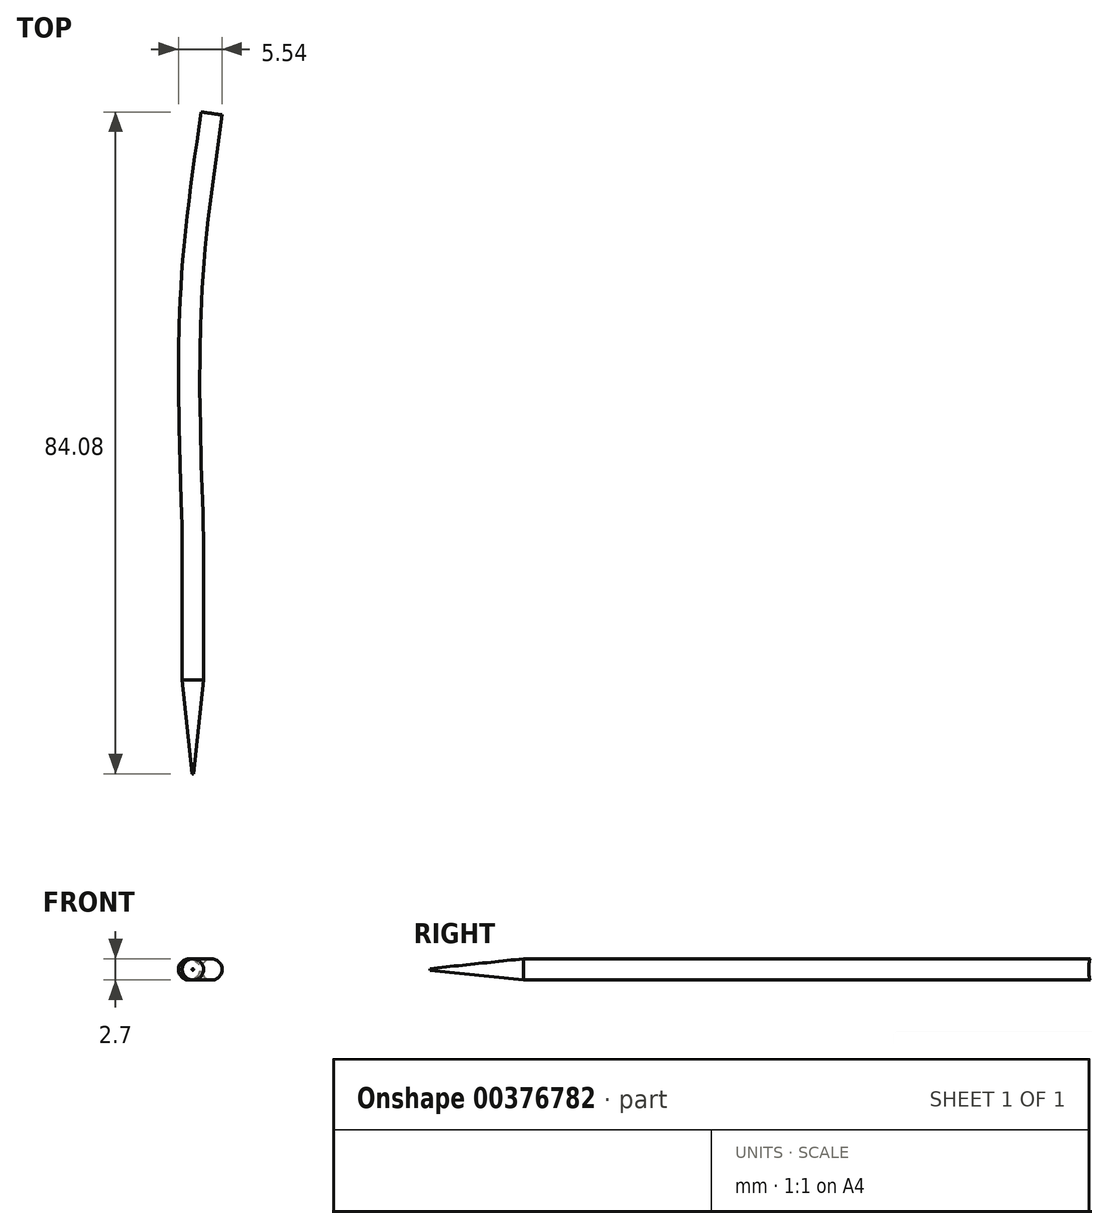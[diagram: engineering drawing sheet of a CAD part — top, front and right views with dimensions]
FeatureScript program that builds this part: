
annotation { "Feature Type Name" : "Feature", "Feature Type Description" : "" }
export const myFeature = defineFeature(function(context is Context, id is Id, definition is map)
    precondition{}
    {
        {
            var Q0;
            Q0=qCreatedBy(makeId("Front.planeOp"),FACE);
            var sketch = newSketch(context, id + "F0", { "sketchPlane" : qUnion([Q0])});
            skCircle(sketch, "E0", {"center": v(0, 0) * mm, "radius": 1.35 * mm});
            skCircle(sketch, "E1.0", {"center": v(0, 0) * mm, "radius": 0.1 * mm});
            skCircle(sketch, "E2.0", {"center": v(0, 0) * mm, "radius": 2.65 * mm});
            skSolve(sketch);
        }
        {
            var Q0;
            Q0=qCreatedBy(makeId("Top.planeOp"),FACE);
            var sketch = newSketch(context, id + "F1", { "sketchPlane" : qUnion([Q0])});
            skLineSegment(sketch, "E3", {"start": v(0, 0) * mm, "end": v(0, 30) * mm});
            skFitSpline(sketch, "E4", {"points": [v(0, 30) * mm, v(-0.41, 56.26) * mm, v(2.37, 83.9) * mm], "startDerivative": vector(0, 15.42) * mm, "endDerivative": vector(7.15, 51.63) * mm});
            skSolve(sketch);
        }
        {
            var Q0;
            Q0=makeQuery(id+"F0.imprint","IMPRINT",FACE,{"disambiguationData":[TD([[makeQuery(id+"F0.imprint","IMPRINT",EDGE,{"derivedFrom":sQuery(id+"F0.wireOp",EDGE,"E0")}),1.0]])]});
            var Q1;
            Q1=makeQuery(id+"F0.imprint","IMPRINT",FACE,{"disambiguationData":[TD([[makeQuery(id+"F0.imprint","IMPRINT",EDGE,{"derivedFrom":sQuery(id+"F0.wireOp",EDGE,"E1.0")}),1.0]])]});
            var Q2;
            Q2=sQuery(id+"F1.wireOp",EDGE,"E3");
            var Q3;
            Q3=sQuery(id+"F1.wireOp",EDGE,"E4");
            sweep(context, id + "F2", {"profiles" : qUnion([Q0, Q1]), "path" : qUnion([Q2, Q3])});
        }
        {
            var Q0;
            Q0=makeQuery(id+"F0.imprint","IMPRINT",FACE,{"disambiguationData":[TD([[makeQuery(id+"F0.imprint","IMPRINT",EDGE,{"derivedFrom":sQuery(id+"F0.wireOp",EDGE,"E0")}),1.0]])]});
            var Q1;
            Q1=makeQuery(id+"F0.imprint","IMPRINT",FACE,{"disambiguationData":[TD([[makeQuery(id+"F0.imprint","IMPRINT",EDGE,{"derivedFrom":sQuery(id+"F0.wireOp",EDGE,"E0")}),-1.0]])]});
            extrude(context, id + "F3", {"entities" : qUnion([Q0, Q1]), "operationType" : NewBodyOperationType.REMOVE, "oppositeDirection" : true, "depth" : 40 * mm, "hasDraft" : true, "draftAngle" : 6 * degree, "draftPullDirection" : true});
        }
    });
